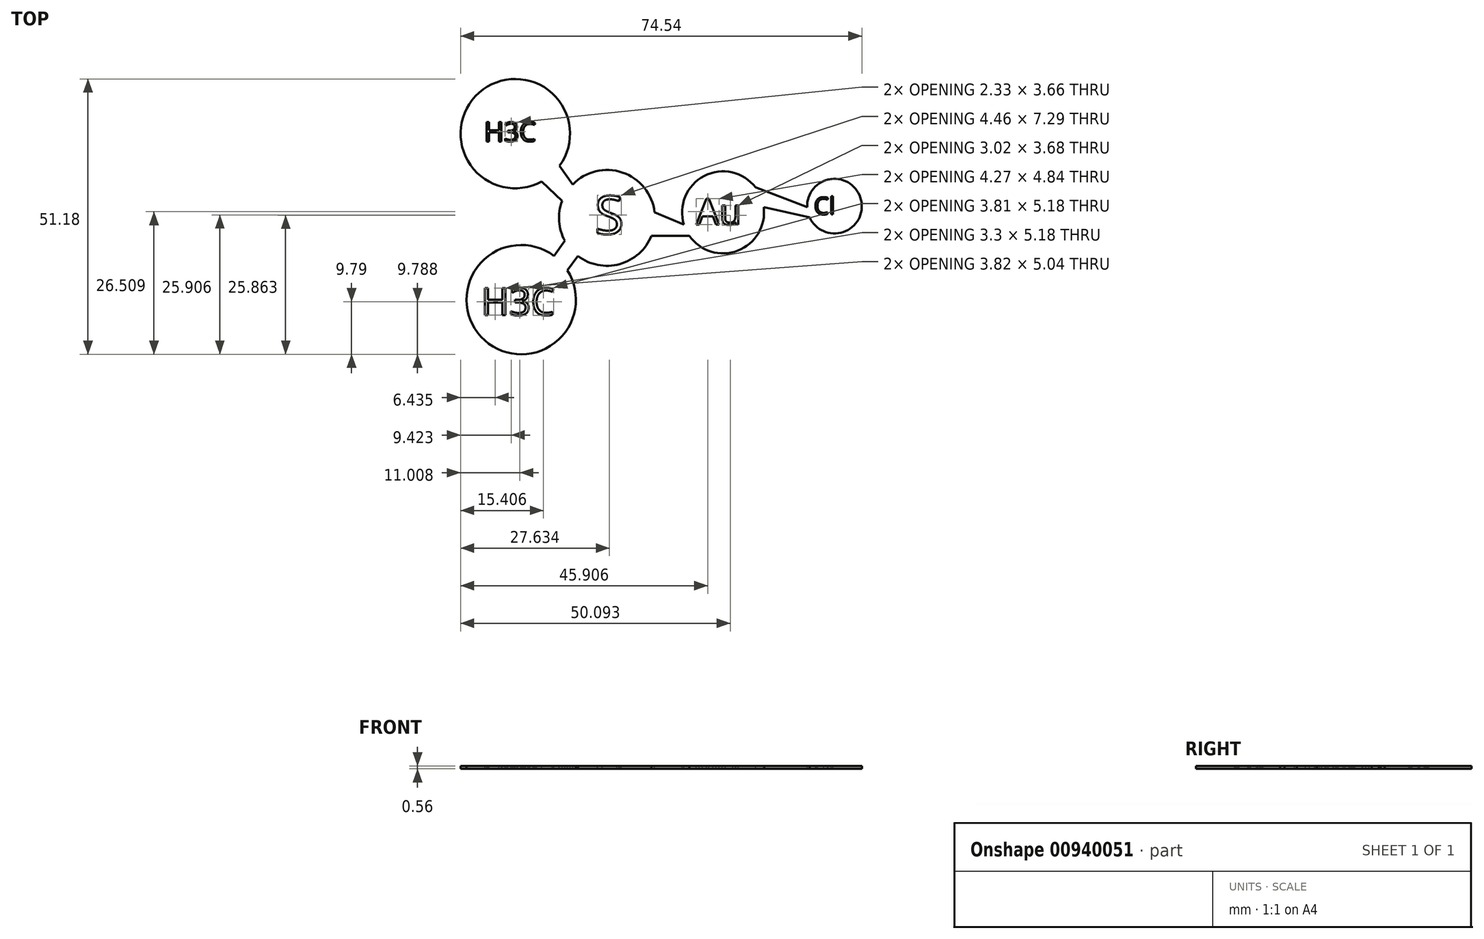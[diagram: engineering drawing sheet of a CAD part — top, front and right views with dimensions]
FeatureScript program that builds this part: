
annotation { "Feature Type Name" : "Feature", "Feature Type Description" : "" }
export const myFeature = defineFeature(function(context is Context, id is Id, definition is map)
    precondition{}
    {
        {
            var Q0;
            Q0=qCreatedBy(makeId("Top.planeOp"),FACE);
            var sketch = newSketch(context, id + "F0", { "sketchPlane" : qUnion([Q0])});
            skCircle(sketch, "E0", {"center": v(-59.7, 45.24) * mm, "radius": 10.16 * mm});
            skCircle(sketch, "E1", {"center": v(-58.61, 14.38) * mm, "radius": 10.16 * mm});
            skCircle(sketch, "E2", {"center": v(-42.67, 29.58) * mm, "radius": 8.9 * mm});
            skCircle(sketch, "E3", {"center": v(-21.11, 30.6) * mm, "radius": 7.62 * mm});
            skText(sketch, "E4", { "text": "H3C", "fontName": "OpenSans-Regular.ttf"});
            skText(sketch, "E5", { "text": "H3C", "fontName": "OpenSans-Regular.ttf"});
            skText(sketch, "E6", { "text": "S", "fontName": "OpenSans-Regular.ttf"});
            skText(sketch, "E7", { "text": "Au", "fontName": "OpenSans-Regular.ttf"});
            skCircle(sketch, "E8", {"center": v(-0.41, 31.76) * mm, "radius": 5.08 * mm});
            skText(sketch, "E9", { "text": "Cl", "fontName": "OpenSans-Regular.ttf"});
            skLineSegment(sketch, "E10", {"start": v(-54.82, 36.33) * mm, "end": v(-51.02, 32.7) * mm});
            skLineSegment(sketch, "E11", {"start": v(-51.02, 32.7) * mm, "end": v(-51.5, 39.26) * mm});
            skLineSegment(sketch, "E12", {"start": v(-51.5, 39.26) * mm, "end": v(-49.06, 35.8) * mm});
            skLineSegment(sketch, "E13", {"start": v(-50.5, 25.33) * mm, "end": v(-52.5, 22.5) * mm});
            skLineSegment(sketch, "E14", {"start": v(-52.5, 22.5) * mm, "end": v(-48.07, 22.5) * mm});
            skLineSegment(sketch, "E15", {"start": v(-48.07, 22.5) * mm, "end": v(-50.05, 19.86) * mm});
            skLineSegment(sketch, "E16", {"start": v(-33.82, 30.62) * mm, "end": v(-28.38, 28.31) * mm});
            skLineSegment(sketch, "E17", {"start": v(-28.38, 28.31) * mm, "end": v(-34.4, 26.26) * mm});
            skLineSegment(sketch, "E18", {"start": v(-34.4, 26.26) * mm, "end": v(-27.37, 26.26) * mm});
            skLineSegment(sketch, "E19", {"start": v(-15.06, 35.23) * mm, "end": v(-5.5, 31.57) * mm});
            skLineSegment(sketch, "E20", {"start": v(-5.5, 31.57) * mm, "end": v(-13.55, 31.57) * mm});
            skLineSegment(sketch, "E21", {"start": v(-13.55, 31.57) * mm, "end": v(-5.04, 29.67) * mm});
            const initialGuessF0  = {"E4": [-0.06552, 0.0438, 1, 0, 0.00359], "E5": [-0.06604, 0.01149, 1, 0, 0.00508], "E6": [-0.04498, 0.02658, 1, 0, 0.00715], "E7": [-0.0261, 0.02831, 1, 0, 0.00486], "E9": [-0.00424, 0.03023, 1, 0, 0.0032]};
            skSetInitialGuess(sketch, initialGuessF0);
            skSolve(sketch);
        }
        {
            var Q0;
            Q0=makeQuery(id+"F0.imprint","IMPRINT",FACE,{"disambiguationData":[TD([[makeQuery(id+"F0.imprint","IMPRINT",EDGE,{"derivedFrom":sQuery(id+"F0.wireOp",EDGE,"E4.sketch_text.stroke-0")}),1.0]])]});
            var Q1;
            Q1=makeQuery(id+"F0.imprint","IMPRINT",FACE,{"disambiguationData":[TD([[makeQuery(id+"F0.imprint","IMPRINT",EDGE,{"derivedFrom":sQuery(id+"F0.wireOp",EDGE,"E6.sketch_text.stroke-0")}),1.0]])]});
            var Q2;
            {var subQ0=sQuery(id+"F0.wireOp",EDGE,"E10");Q2=makeQuery(id+"F0.imprint","IMPRINT",FACE,{"disambiguationData":[TD([[makeQuery(id+"F0.imprint","IMPRINT",EDGE,{"derivedFrom":subQ0}),1.0]])]});}
            var Q3;
            {var subQ0=sQuery(id+"F0.wireOp",EDGE,"E11");Q3=makeQuery(id+"F0.imprint","IMPRINT",FACE,{"disambiguationData":[TD([[makeQuery(id+"F0.imprint","IMPRINT",EDGE,{"derivedFrom":subQ0}),-1.0]])]});}
            var Q4;
            {var subQ0=sQuery(id+"F0.wireOp",EDGE,"E13");Q4=makeQuery(id+"F0.imprint","IMPRINT",FACE,{"disambiguationData":[TD([[makeQuery(id+"F0.imprint","IMPRINT",EDGE,{"derivedFrom":subQ0}),1.0]])]});}
            var Q5;
            {var subQ0=sQuery(id+"F0.wireOp",EDGE,"E14");Q5=makeQuery(id+"F0.imprint","IMPRINT",FACE,{"disambiguationData":[TD([[makeQuery(id+"F0.imprint","IMPRINT",EDGE,{"derivedFrom":subQ0}),-1.0]])]});}
            var Q6;
            Q6=makeQuery(id+"F0.imprint","IMPRINT",FACE,{"disambiguationData":[TD([[makeQuery(id+"F0.imprint","IMPRINT",EDGE,{"derivedFrom":sQuery(id+"F0.wireOp",EDGE,"E5.sketch_text.stroke-0")}),1.0]])]});
            var Q7;
            Q7=makeQuery(id+"F0.imprint","IMPRINT",FACE,{"disambiguationData":[TD([[makeQuery(id+"F0.imprint","IMPRINT",EDGE,{"derivedFrom":sQuery(id+"F0.wireOp",EDGE,"E7.sketch_text.stroke-0")}),1.0]])]});
            var Q8;
            {var subQ0=sQuery(id+"F0.wireOp",EDGE,"E16");Q8=makeQuery(id+"F0.imprint","IMPRINT",FACE,{"disambiguationData":[TD([[makeQuery(id+"F0.imprint","IMPRINT",EDGE,{"derivedFrom":subQ0}),-1.0]])]});}
            var Q9;
            {var subQ0=sQuery(id+"F0.wireOp",EDGE,"E17");Q9=makeQuery(id+"F0.imprint","IMPRINT",FACE,{"disambiguationData":[TD([[makeQuery(id+"F0.imprint","IMPRINT",EDGE,{"derivedFrom":subQ0}),1.0]])]});}
            var Q10;
            {var subQ0=sQuery(id+"F0.wireOp",EDGE,"E19");Q10=makeQuery(id+"F0.imprint","IMPRINT",FACE,{"disambiguationData":[TD([[makeQuery(id+"F0.imprint","IMPRINT",EDGE,{"derivedFrom":subQ0}),-1.0]])]});}
            var Q11;
            {var subQ0=sQuery(id+"F0.wireOp",EDGE,"E20");Q11=makeQuery(id+"F0.imprint","IMPRINT",FACE,{"disambiguationData":[TD([[makeQuery(id+"F0.imprint","IMPRINT",EDGE,{"derivedFrom":subQ0}),1.0]])]});}
            var Q12;
            Q12=makeQuery(id+"F0.imprint","IMPRINT",FACE,{"disambiguationData":[TD([[makeQuery(id+"F0.imprint","IMPRINT",EDGE,{"derivedFrom":sQuery(id+"F0.wireOp",EDGE,"E9.sketch_text.stroke-0")}),1.0]])]});
            extrude(context, id + "F1", {"entities" : qUnion([Q0, Q1, Q2, Q3, Q4, Q5, Q6, Q7, Q8, Q9, Q10, Q11, Q12]), "oppositeDirection" : true, "depth" : 0.56 * mm, "offsetDistance" : 25.4 * mm});
        }
    });
